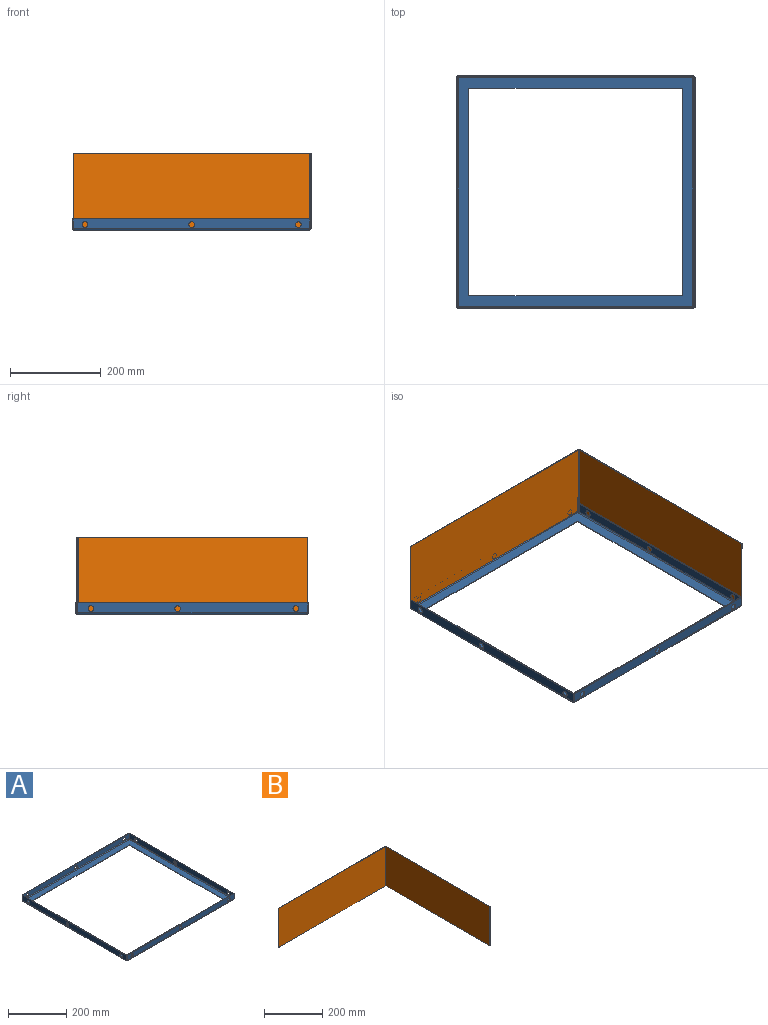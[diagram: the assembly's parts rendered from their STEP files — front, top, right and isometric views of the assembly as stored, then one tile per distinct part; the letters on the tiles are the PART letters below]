
ASSEMBLY  parts=2 mates=1
PART A: 62 faces, bbox 523.9x511.2x25.4 mm
  f0: plane 457.2x1.59mm, normal (-1,0,0), area 725.8mm2, adj f1,f3,f4,f5
  f1: plane 469.9x1.59mm, normal (0,-1,0), area 746mm2, adj f0,f2,f4,f5
  f2: plane 457.2x1.59mm, normal (1,0,0), area 725.8mm2, adj f1,f3,f4,f5
  f3: plane 469.9x1.59mm, normal (0,1,0), area 746mm2, adj f0,f2,f4,f5
  f4: plane 516.13x503.43mm, normal (0,0,-1), area 44995mm2, adj f0,f1,f2,f3,f18,f32,f46,f60
  f5: plane 516.13x503.43mm, normal (0,0,1), area 44995mm2, adj f0,f1,f2,f3,f19,f33,f47,f61
  f6: plane 2.26x1.59mm, normal (0,0,-1), area 3.6mm2, adj f8,f14,f15,f17
  f7: plane 520.65x1.59mm, normal (0,0,1), area 826.5mm2, adj f8,f13,f14,f15
  f8: plane 21.53x1.59mm, normal (-1,0,0), area 34.2mm2, adj f6,f7,f14,f15
  f9: plane 2.26x1.59mm, normal (0,0,-1), area 3.6mm2, adj f13,f14,f15,f16
  f10: cylinder r=6.35mm len=12.7mm, axis (0,-1,0), area 63.3mm2, adj f14,f15
  f11: cylinder r=6.35mm len=12.7mm, axis (0,-1,0), area 63.3mm2, adj f14,f15
  f12: cylinder r=6.35mm len=12.7mm, axis (0,-1,0), area 63.3mm2, adj f14,f15
  f13: plane 21.53x1.59mm, normal (1,0,0), area 34.2mm2, adj f7,f9,f14,f15
  f14: plane 520.65x21.53mm, normal (0,-1,0), area 10827.7mm2, adj f6,f7,f8,f9,f10,f11,f12,f13
  f15: plane 520.65x21.53mm, normal (0,1,0), area 10827.7mm2, adj f6,f7,f8,f9,f10,f11,f12,f13
  f16: plane 3.87x3.87mm, normal (1,0,0), area 7.7mm2, adj f9,f18,f19,f58
  f17: plane 3.87x3.87mm, normal (-1,0,0), area 7.7mm2, adj f6,f18,f19,f30
  f18: cylinder r=3.87mm len=516.13mm, axis (1,0,0), area 3140.4mm2, adj f4,f14,f16,f17
  f19: cylinder r=2.29mm len=516.13mm, axis (1,0,0), area 1853.3mm2, adj f5,f15,f16,f17
  f20: plane 2.26x1.59mm, normal (0,0,-1), area 3.6mm2, adj f22,f28,f29,f31
  f21: plane 507.95x1.59mm, normal (0,0,1), area 806.4mm2, adj f22,f27,f28,f29
  f22: plane 21.53x1.59mm, normal (0,1,0), area 34.2mm2, adj f20,f21,f28,f29
  f23: plane 2.26x1.59mm, normal (0,0,-1), area 3.6mm2, adj f27,f28,f29,f30
  f24: cylinder r=6.35mm len=12.7mm, axis (-1,0,0), area 63.3mm2, adj f28,f29
  f25: cylinder r=6.35mm len=12.7mm, axis (-1,0,0), area 63.3mm2, adj f28,f29
  f26: cylinder r=6.35mm len=12.7mm, axis (-1,0,0), area 63.3mm2, adj f28,f29
  f27: plane 21.53x1.59mm, normal (0,-1,0), area 34.2mm2, adj f21,f23,f28,f29
  f28: plane 507.95x21.53mm, normal (-1,0,0), area 10554.3mm2, adj f20,f21,f22,f23,f24,f25,f26,f27
  f29: plane 507.95x21.53mm, normal (1,0,0), area 10554.3mm2, adj f20,f21,f22,f23,f24,f25,f26,f27
  f30: plane 3.87x3.87mm, normal (0,-1,0), area 7.7mm2, adj f17,f23,f32,f33
  f31: plane 3.87x3.87mm, normal (0,1,0), area 7.7mm2, adj f20,f32,f33,f45
  f32: cylinder r=3.87mm len=503.43mm, axis (0,-1,0), area 3063.1mm2, adj f4,f28,f30,f31
  f33: cylinder r=2.29mm len=503.43mm, axis (0,-1,0), area 1807.7mm2, adj f5,f29,f30,f31
  f34: plane 2.26x1.59mm, normal (0,0,-1), area 3.6mm2, adj f36,f42,f43,f44
  f35: plane 520.65x1.59mm, normal (0,0,1), area 826.5mm2, adj f36,f41,f42,f43
  f36: plane 21.53x1.59mm, normal (1,0,0), area 34.2mm2, adj f34,f35,f42,f43
  f37: plane 2.26x1.59mm, normal (0,0,-1), area 3.6mm2, adj f41,f42,f43,f45
  f38: cylinder r=6.35mm len=12.7mm, axis (0,1,0), area 63.3mm2, adj f42,f43
  f39: cylinder r=6.35mm len=12.7mm, axis (0,1,0), area 63.3mm2, adj f42,f43
  f40: cylinder r=6.35mm len=12.7mm, axis (0,1,0), area 63.3mm2, adj f42,f43
  f41: plane 21.53x1.59mm, normal (-1,0,0), area 34.2mm2, adj f35,f37,f42,f43
  f42: plane 520.65x21.53mm, normal (0,1,0), area 10827.7mm2, adj f34,f35,f36,f37,f38,f39,f40,f41
  f43: plane 520.65x21.53mm, normal (0,-1,0), area 10827.7mm2, adj f34,f35,f36,f37,f38,f39,f40,f41
  f44: plane 3.87x3.87mm, normal (1,0,0), area 7.7mm2, adj f34,f46,f47,f59
  f45: plane 3.87x3.87mm, normal (-1,0,0), area 7.7mm2, adj f31,f37,f46,f47
  f46: cylinder r=3.87mm len=516.13mm, axis (1,0,0), area 3140.4mm2, adj f4,f42,f44,f45
  f47: cylinder r=2.29mm len=516.13mm, axis (1,0,0), area 1853.3mm2, adj f5,f43,f44,f45
  f48: plane 2.26x1.59mm, normal (0,0,-1), area 3.6mm2, adj f50,f56,f57,f58
  f49: plane 507.95x1.59mm, normal (0,0,1), area 806.4mm2, adj f50,f55,f56,f57
  f50: plane 21.53x1.59mm, normal (0,-1,0), area 34.2mm2, adj f48,f49,f56,f57
  f51: plane 2.26x1.59mm, normal (0,0,-1), area 3.6mm2, adj f55,f56,f57,f59
  f52: cylinder r=6.35mm len=12.7mm, axis (1,0,0), area 63.3mm2, adj f56,f57
  f53: cylinder r=6.35mm len=12.7mm, axis (1,0,0), area 63.3mm2, adj f56,f57
  f54: cylinder r=6.35mm len=12.7mm, axis (1,0,0), area 63.3mm2, adj f56,f57
  f55: plane 21.53x1.59mm, normal (0,1,0), area 34.2mm2, adj f49,f51,f56,f57
  f56: plane 507.95x21.53mm, normal (1,0,0), area 10554.3mm2, adj f48,f49,f50,f51,f52,f53,f54,f55
  f57: plane 507.95x21.53mm, normal (-1,0,0), area 10554.3mm2, adj f48,f49,f50,f51,f52,f53,f54,f55
  f58: plane 3.87x3.87mm, normal (0,-1,0), area 7.7mm2, adj f16,f48,f60,f61
  f59: plane 3.87x3.87mm, normal (0,1,0), area 7.7mm2, adj f44,f51,f60,f61
  f60: cylinder r=3.87mm len=503.43mm, axis (0,-1,0), area 3063.1mm2, adj f4,f56,f58,f59
  f61: cylinder r=2.29mm len=503.43mm, axis (0,-1,0), area 1807.7mm2, adj f5,f57,f58,f59
PART B: 14 faces, bbox 524.5x507.9x165.1 mm
  f0: plane 520.65x1.59mm, normal (0,0,1), area 826.5mm2, adj f2,f3,f4,f10
  f1: plane 520.65x1.59mm, normal (0,0,-1), area 826.5mm2, adj f2,f3,f4,f11
  f2: plane 165.1x1.59mm, normal (-1,0,0), area 262.1mm2, adj f0,f1,f3,f4
  f3: plane 520.65x165.1mm, normal (0,1,0), area 85959.2mm2, adj f0,f1,f2,f12
  f4: plane 520.65x165.1mm, normal (0,-1,0), area 85959.2mm2, adj f0,f1,f2,f13
  f5: plane 165.1x1.59mm, normal (0,-1,0), area 262.1mm2, adj f6,f7,f8,f9
  f6: plane 504.08x1.59mm, normal (0,0,-1), area 800.2mm2, adj f5,f8,f9,f11
  f7: plane 504.08x1.59mm, normal (0,0,1), area 800.2mm2, adj f5,f8,f9,f10
  f8: plane 504.08x165.1mm, normal (1,0,0), area 83222.9mm2, adj f5,f6,f7,f12
  f9: plane 504.08x165.1mm, normal (-1,0,0), area 83222.9mm2, adj f5,f6,f7,f13
  f10: plane 3.87x3.87mm, normal (0,0,1), area 7.7mm2, adj f0,f7,f12,f13
  f11: plane 3.87x3.87mm, normal (0,0,-1), area 7.7mm2, adj f1,f6,f12,f13
  f12: cylinder r=3.87mm len=165.1mm, axis (0,0,1), area 1004.5mm2, adj f3,f8,f10,f11
  f13: cylinder r=2.29mm len=165.1mm, axis (0,0,1), area 592.8mm2, adj f4,f9,f10,f11
PLACE A t=(-0.49,1.5,0)mm
PLACE B t=(92.7,375.7,104.44)mm
MATE fastened B.f6 <-> A.f48  axis (0,0,-1) through (349.56,-132.25,3.87)mm
